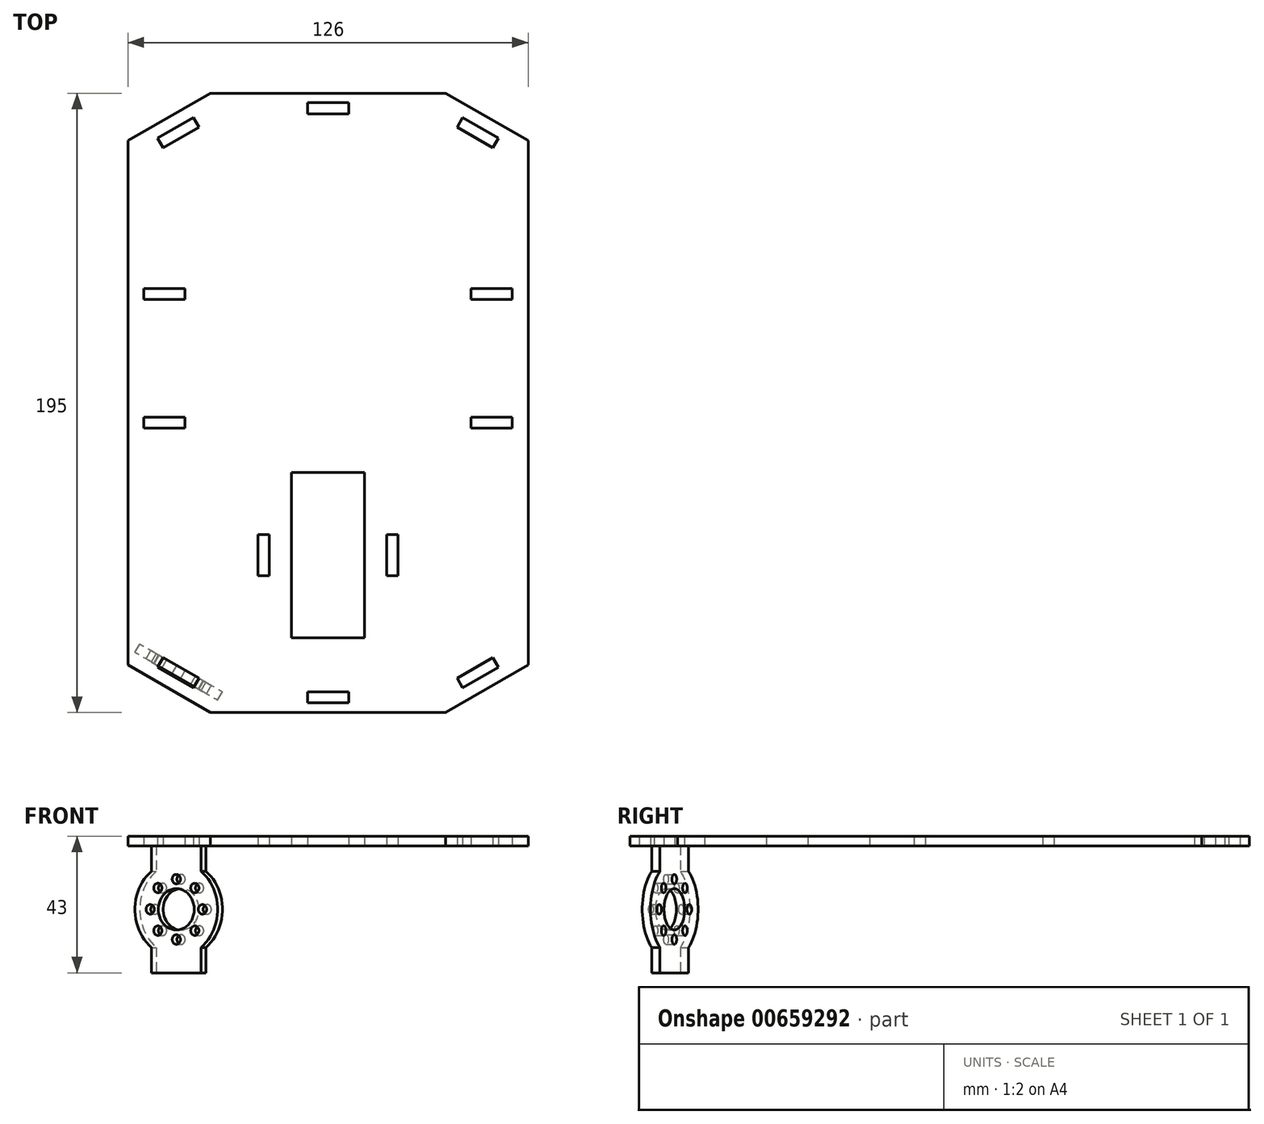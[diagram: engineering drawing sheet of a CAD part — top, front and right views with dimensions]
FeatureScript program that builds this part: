
annotation { "Feature Type Name" : "Feature", "Feature Type Description" : "" }
export const myFeature = defineFeature(function(context is Context, id is Id, definition is map)
    precondition{}
    {
        {
            var Q0;
            Q0=qCreatedBy(makeId("Top.planeOp"),FACE);
            var sketch = newSketch(context, id + "F0", { "sketchPlane" : qUnion([Q0])});
            skLineSegment(sketch, "E0.bottom", {"start": v(-63, 97.5) * mm, "end": v(63, 97.5) * mm});
            skLineSegment(sketch, "E0.top", {"start": v(-63, -97.5) * mm, "end": v(63, -97.5) * mm});
            skLineSegment(sketch, "E0.left", {"start": v(-63, 97.5) * mm, "end": v(-63, -97.5) * mm});
            skLineSegment(sketch, "E0.right", {"start": v(63, 97.5) * mm, "end": v(63, -97.5) * mm});
            skPoint(sketch, "E0.middle", {"position": v(0, 0) * mm});
            skLineSegment(sketch, "E1", {"start": v(-37, 97.5) * mm, "end": v(-63, 82.53) * mm});
            skLineSegment(sketch, "E2", {"start": v(37, 97.5) * mm, "end": v(63, 82.53) * mm});
            skLineSegment(sketch, "E3", {"start": v(-63, 0) * mm, "end": v(63, 0) * mm, "construction": true});
            skLineSegment(sketch, "E4.MirrorCS", {"start": v(-37, -97.5) * mm, "end": v(-63, -82.53) * mm});
            skLineSegment(sketch, "E5.MirrorCS", {"start": v(37, -97.5) * mm, "end": v(63, -82.53) * mm});
            skPoint(sketch, "E6", {"position": v(0, 97.5) * mm});
            skLineSegment(sketch, "E7.bottom", {"start": v(-6.5, 91) * mm, "end": v(6.5, 91) * mm});
            skLineSegment(sketch, "E7.top", {"start": v(-6.5, 94.5) * mm, "end": v(6.5, 94.5) * mm});
            skLineSegment(sketch, "E7.left", {"start": v(-6.5, 91) * mm, "end": v(-6.5, 94.5) * mm});
            skLineSegment(sketch, "E7.right", {"start": v(6.5, 91) * mm, "end": v(6.5, 94.5) * mm});
            skPoint(sketch, "E7.middle", {"position": v(0, 92.75) * mm});
            skPoint(sketch, "E8.MirrorP", {"position": v(0, -97.5) * mm});
            skLineSegment(sketch, "E9.MirrorCS", {"start": v(6.5, -91) * mm, "end": v(6.5, -94.5) * mm});
            skLineSegment(sketch, "E10.MirrorCS", {"start": v(-6.5, -91) * mm, "end": v(-6.5, -94.5) * mm});
            skLineSegment(sketch, "E11.MirrorCS", {"start": v(-6.5, -94.5) * mm, "end": v(6.5, -94.5) * mm});
            skLineSegment(sketch, "E12.MirrorCS", {"start": v(-6.5, -91) * mm, "end": v(6.5, -91) * mm});
            skPoint(sketch, "E13.MirrorP", {"position": v(0, -92.75) * mm});
            skLineSegment(sketch, "E14.bottom", {"start": v(-11.5, -22) * mm, "end": v(11.5, -22) * mm});
            skLineSegment(sketch, "E14.top", {"start": v(-11.5, -74) * mm, "end": v(11.5, -74) * mm});
            skLineSegment(sketch, "E14.left", {"start": v(-11.5, -22) * mm, "end": v(-11.5, -74) * mm});
            skLineSegment(sketch, "E14.right", {"start": v(11.5, -22) * mm, "end": v(11.5, -74) * mm});
            skPoint(sketch, "E14.middle", {"position": v(0, -48) * mm});
            skLineSegment(sketch, "E15.bottom", {"start": v(18.5, -41.5) * mm, "end": v(22, -41.5) * mm});
            skLineSegment(sketch, "E15.top", {"start": v(18.5, -54.5) * mm, "end": v(22, -54.5) * mm});
            skLineSegment(sketch, "E15.left", {"start": v(18.5, -41.5) * mm, "end": v(18.5, -54.5) * mm});
            skLineSegment(sketch, "E15.right", {"start": v(22, -41.5) * mm, "end": v(22, -54.5) * mm});
            skPoint(sketch, "E15.middle", {"position": v(20.25, -48) * mm});
            skLineSegment(sketch, "E16.bottom", {"start": v(-22, -41.5) * mm, "end": v(-18.5, -41.5) * mm});
            skLineSegment(sketch, "E16.top", {"start": v(-22, -54.5) * mm, "end": v(-18.5, -54.5) * mm});
            skLineSegment(sketch, "E16.left", {"start": v(-22, -41.5) * mm, "end": v(-22, -54.5) * mm});
            skLineSegment(sketch, "E16.right", {"start": v(-18.5, -41.5) * mm, "end": v(-18.5, -54.5) * mm});
            skPoint(sketch, "E16.middle", {"position": v(-20.25, -48) * mm});
            skLineSegment(sketch, "E17.bottom", {"start": v(-58, 36) * mm, "end": v(-45, 36) * mm});
            skLineSegment(sketch, "E17.top", {"start": v(-58, 32.5) * mm, "end": v(-45, 32.5) * mm});
            skLineSegment(sketch, "E17.left", {"start": v(-58, 36) * mm, "end": v(-58, 32.5) * mm});
            skLineSegment(sketch, "E17.right", {"start": v(-45, 36) * mm, "end": v(-45, 32.5) * mm});
            skLineSegment(sketch, "E18.bottom", {"start": v(-58, -4.5) * mm, "end": v(-45, -4.5) * mm});
            skLineSegment(sketch, "E18.top", {"start": v(-58, -8) * mm, "end": v(-45, -8) * mm});
            skLineSegment(sketch, "E18.left", {"start": v(-58, -4.5) * mm, "end": v(-58, -8) * mm});
            skLineSegment(sketch, "E18.right", {"start": v(-45, -4.5) * mm, "end": v(-45, -8) * mm});
            skLineSegment(sketch, "E19.MirrorCS", {"start": v(45, 36) * mm, "end": v(45, 32.5) * mm});
            skLineSegment(sketch, "E20.MirrorCS", {"start": v(45, -4.5) * mm, "end": v(45, -8) * mm});
            skLineSegment(sketch, "E21.MirrorCS", {"start": v(58, -4.5) * mm, "end": v(58, -8) * mm});
            skLineSegment(sketch, "E22.MirrorCS", {"start": v(58, 36) * mm, "end": v(58, 32.5) * mm});
            skLineSegment(sketch, "E23.MirrorCS", {"start": v(58, -4.5) * mm, "end": v(45, -4.5) * mm});
            skLineSegment(sketch, "E24.MirrorCS", {"start": v(58, 32.5) * mm, "end": v(45, 32.5) * mm});
            skLineSegment(sketch, "E25.MirrorCS", {"start": v(58, 36) * mm, "end": v(45, 36) * mm});
            skLineSegment(sketch, "E26.MirrorCS", {"start": v(58, -8) * mm, "end": v(45, -8) * mm});
            skLineSegment(sketch, "E27", {"start": v(63, 82.53) * mm, "end": v(63, -82.53) * mm, "construction": true});
            skLineSegment(sketch, "E28", {"start": v(-63, 82.53) * mm, "end": v(-63, -82.53) * mm, "construction": true});
            skLineSegment(sketch, "E29", {"start": v(-42.37, 89.8) * mm, "end": v(-53.64, 83.3) * mm});
            skLineSegment(sketch, "E30", {"start": v(-42.37, 89.8) * mm, "end": v(-40.63, 86.76) * mm});
            skLineSegment(sketch, "E31", {"start": v(-40.63, 86.76) * mm, "end": v(-51.9, 80.27) * mm});
            skLineSegment(sketch, "E32", {"start": v(-51.9, 80.27) * mm, "end": v(-53.64, 83.3) * mm});
            skLineSegment(sketch, "E33", {"start": v(-37, 97.5) * mm, "end": v(-42.37, 89.8) * mm, "construction": true});
            skLineSegment(sketch, "E34", {"start": v(-63, 82.53) * mm, "end": v(-53.64, 83.3) * mm, "construction": true});
            skLineSegment(sketch, "E35.MirrorCS", {"start": v(42.37, 89.8) * mm, "end": v(53.64, 83.3) * mm});
            skLineSegment(sketch, "E36.MirrorCS", {"start": v(42.37, 89.8) * mm, "end": v(40.63, 86.76) * mm});
            skLineSegment(sketch, "E37.MirrorCS", {"start": v(40.63, 86.76) * mm, "end": v(51.9, 80.27) * mm});
            skLineSegment(sketch, "E38.MirrorCS", {"start": v(51.9, 80.27) * mm, "end": v(53.64, 83.3) * mm});
            skLineSegment(sketch, "E39.MirrorCS", {"start": v(42.37, -89.8) * mm, "end": v(53.64, -83.3) * mm});
            skLineSegment(sketch, "E40.MirrorCS", {"start": v(40.63, -86.76) * mm, "end": v(51.9, -80.27) * mm});
            skLineSegment(sketch, "E41.MirrorCS", {"start": v(42.37, -89.8) * mm, "end": v(40.63, -86.76) * mm});
            skLineSegment(sketch, "E42.MirrorCS", {"start": v(51.9, -80.27) * mm, "end": v(53.64, -83.3) * mm});
            skLineSegment(sketch, "E43.MirrorCS", {"start": v(-42.37, -89.8) * mm, "end": v(-53.64, -83.3) * mm});
            skLineSegment(sketch, "E44.MirrorCS", {"start": v(-40.63, -86.76) * mm, "end": v(-51.9, -80.27) * mm});
            skLineSegment(sketch, "E45.MirrorCS", {"start": v(-42.37, -89.8) * mm, "end": v(-40.63, -86.76) * mm});
            skLineSegment(sketch, "E46.MirrorCS", {"start": v(-51.9, -80.27) * mm, "end": v(-53.64, -83.3) * mm});
            skSolve(sketch);
        }
        {
            var Q0;
            {var subQ3=sQuery(id+"F0.wireOp",EDGE,"E1");Q0=makeQuery(id+"F0.imprint","IMPRINT",FACE,{"disambiguationData":[TD([[makeQuery(id+"F0.imprint","IMPRINT",EDGE,{"derivedFrom":subQ3}),1.0]])]});}
            extrude(context, id + "F1", {"entities" : qUnion([Q0]), "depth" : 3 * mm, "offsetDistance" : 25 * mm});
        }
        {
            var Q0;
            Q0=makeQuery(id+"F1.opExtrude","SWEPT_FACE",FACE,{"disambiguationData":[OSD([sQuery(id+"F0.wireOp",EDGE,"E44.MirrorCS")])]});
            var sketch = newSketch(context, id + "F2", { "sketchPlane" : qUnion([Q0])});
            skCircle(sketch, "E47", {"center": v(1.57, -20) * mm, "radius": 15 * mm});
            skPoint(sketch, "E47.centerSnap0", {"position": v(1.57, 0) * mm});
            skCircle(sketch, "E48", {"center": v(1.57, -20) * mm, "radius": 6.5 * mm});
            skLineSegment(sketch, "E49.bottom", {"start": v(-7.43, 0) * mm, "end": v(10.57, 0) * mm});
            skLineSegment(sketch, "E49.top", {"start": v(-7.43, -8) * mm, "end": v(10.57, -8) * mm});
            skLineSegment(sketch, "E49.left", {"start": v(-7.43, 0) * mm, "end": v(-7.43, -8) * mm});
            skLineSegment(sketch, "E49.right", {"start": v(10.57, 0) * mm, "end": v(10.57, -8) * mm});
            skLineSegment(sketch, "E50.bottom", {"start": v(-7.43, -32) * mm, "end": v(10.57, -32) * mm});
            skLineSegment(sketch, "E50.top", {"start": v(-7.43, -40) * mm, "end": v(10.57, -40) * mm});
            skLineSegment(sketch, "E50.left", {"start": v(-7.43, -32) * mm, "end": v(-7.43, -40) * mm});
            skLineSegment(sketch, "E50.right", {"start": v(10.57, -32) * mm, "end": v(10.57, -40) * mm});
            skLineSegment(sketch, "E51", {"start": v(1.57, -20) * mm, "end": v(16.57, -20) * mm, "construction": true});
            skCircle(sketch, "E52", {"center": v(1.57, -10.5) * mm, "radius": 1.5 * mm});
            skCircle(sketch, "E53.1.0", {"center": v(-5.14, -13.28) * mm, "radius": 1.5 * mm});
            skCircle(sketch, "E53.2.0", {"center": v(-7.93, -20) * mm, "radius": 1.5 * mm});
            skCircle(sketch, "E53.3.0", {"center": v(-5.14, -26.72) * mm, "radius": 1.5 * mm});
            skCircle(sketch, "E53.4.0", {"center": v(1.57, -29.5) * mm, "radius": 1.5 * mm});
            skCircle(sketch, "E53.5.0", {"center": v(8.3, -26.72) * mm, "radius": 1.5 * mm});
            skCircle(sketch, "E53.6.0", {"center": v(11.07, -20) * mm, "radius": 1.5 * mm});
            skCircle(sketch, "E53.7.0", {"center": v(8.3, -13.28) * mm, "radius": 1.5 * mm});
            skSolve(sketch);
        }
        {
            var Q0;
            {var subQ5=sQuery(id+"F2.wireOp",EDGE,"E49.left");Q0=makeQuery(id+"F2.imprint","IMPRINT",FACE,{"disambiguationData":[TD([[makeQuery(id+"F2.imprint","IMPRINT",EDGE,{"derivedFrom":subQ5}),1.0]])]});}
            var Q1;
            {var subQ0=sQuery(id+"F2.wireOp",EDGE,"E49.top");Q1=makeQuery(id+"F2.imprint","IMPRINT",FACE,{"disambiguationData":[TD([[makeQuery(id+"F2.imprint","IMPRINT",EDGE,{"derivedFrom":subQ0}),1.0]])]});}
            var Q2;
            Q2=makeQuery(id+"F2.imprint","IMPRINT",FACE,{"disambiguationData":[TD([[makeQuery(id+"F2.imprint","IMPRINT",EDGE,{"derivedFrom":sQuery(id+"F2.wireOp",EDGE,"E48")}),-1.0]])]});
            var Q3;
            {var subQ0=sQuery(id+"F2.wireOp",EDGE,"E50.bottom");Q3=makeQuery(id+"F2.imprint","IMPRINT",FACE,{"disambiguationData":[TD([[makeQuery(id+"F2.imprint","IMPRINT",EDGE,{"derivedFrom":subQ0}),-1.0]])]});}
            var Q4;
            Q4=makeQuery(id+"F2.imprint","IMPRINT",FACE,{"disambiguationData":[TD([[makeQuery(id+"F2.imprint","IMPRINT",EDGE,{"derivedFrom":sQuery(id+"F2.wireOp",EDGE,"E50.top")}),1.0]])]});
            extrude(context, id + "F3", {"entities" : qUnion([Q0, Q1, Q2, Q3, Q4]), "depth" : 3 * mm, "offsetDistance" : 25 * mm});
        }
    });
